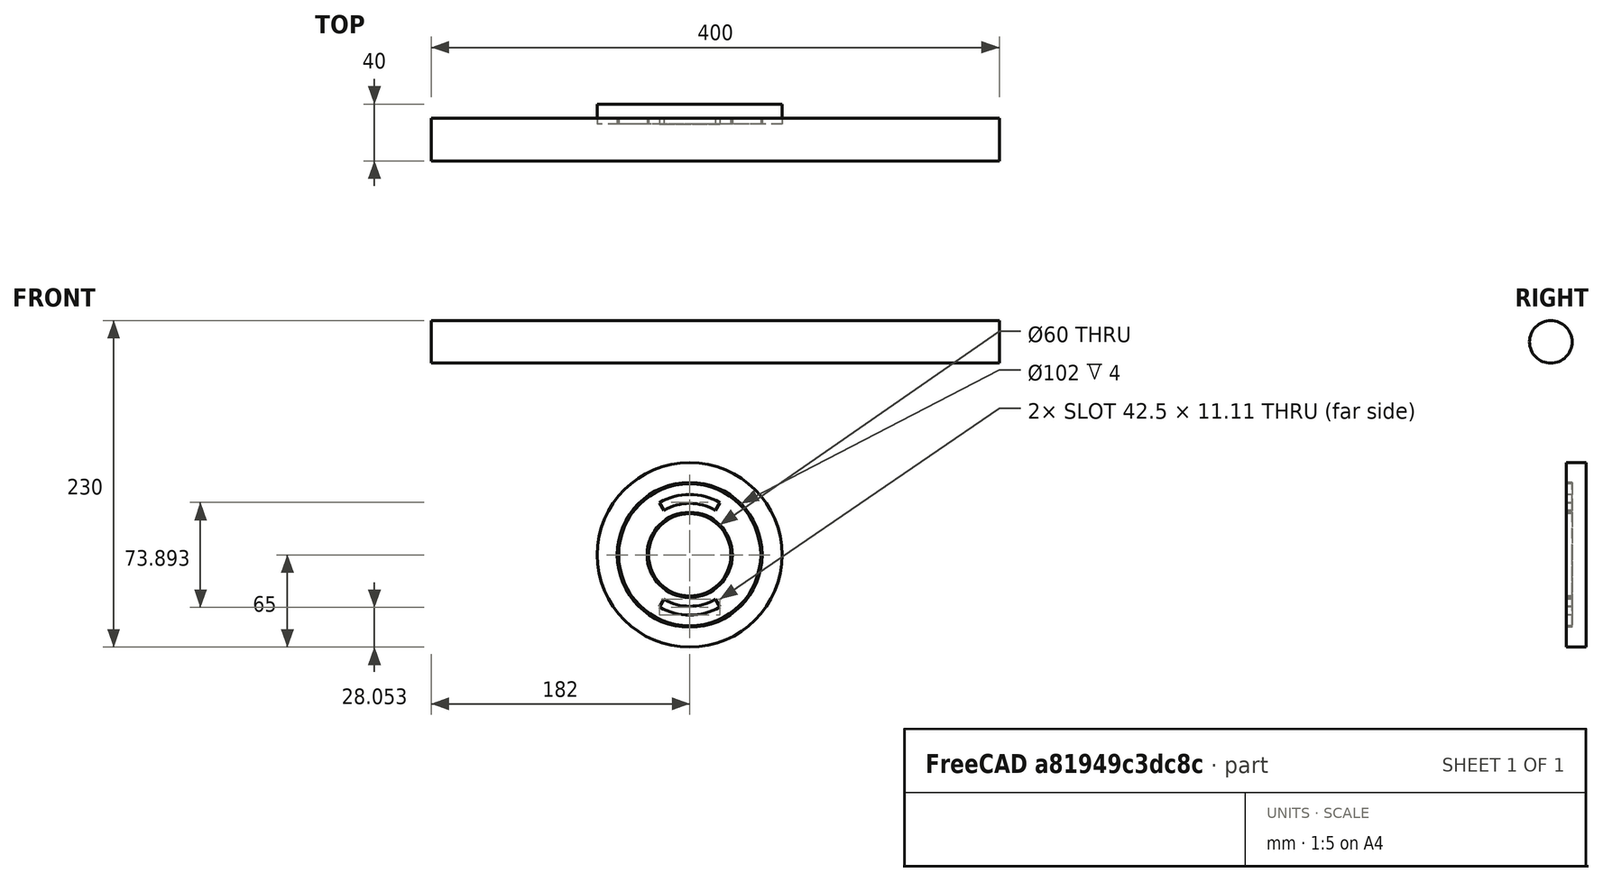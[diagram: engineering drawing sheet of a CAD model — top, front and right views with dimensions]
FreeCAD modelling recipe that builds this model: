
FCSTD DOCUMENT  (FreeCAD 0.19R24276 (Git))
Label: cameraMount
License: All rights reserved
LicenseURL: http://en.wikipedia.org/wiki/All_rights_reserved
objects: Part::Cylinder×9, Part::Cut×4, Part::MultiFuse×2, Part::FeaturePython×1
note: 16 computed .brp shape members not serialized (recipe doc carries the construction recipe); baked Part::Feature solids carry a one-line shape summary decoded from their .brp

FEATURE [Part::Cylinder] Cylinder  label="hor"
  Angle = 360
  AttacherType = Attacher::AttachEngine3D
  Height = 400
  Placement = pos=(0,0,150) rot=(0.707107,0,0.707107;3.14159rad)
  Radius = 15
FEATURE [Part::Cylinder] Cylinder001  label="Cylinder"
  Angle = 360
  AttacherType = Attacher::AttachEngine3D
  Height = 4
  Placement = pos=(182,-19,-4.2e-15) rot=(-1,0,0;4.71239rad)
  Radius = 50
FEATURE [Part::Cylinder] Cylinder002
  Angle = 360
  AttacherType = Attacher::AttachEngine3D
  Height = 4.5
  Placement = pos=(182,-19,-4e-15) rot=(1,0,0;1.5708rad)
  Radius = 30
FEATURE [Part::Cut] Cut  label="cameraPlate"
  Base = -> Cylinder001
  Tool = -> Cylinder002
FEATURE [Part::Cylinder] Cylinder003
  Angle = 60
  AttacherType = Attacher::AttachEngine3D
  Height = 4.5
  Placement = pos=(182,-19,-4e-15) rot=(-0.377964,-0.654654,0.654654;3.86433rad)
  Radius = 36.25
FEATURE [Part::Cylinder] Cylinder004
  Angle = 60
  AttacherType = Attacher::AttachEngine3D
  Height = 4.5
  Placement = pos=(182,-19,-4e-15) rot=(-0.377964,-0.654654,0.654654;3.86433rad)
  Radius = 42.5
FEATURE [Part::Cylinder] Cylinder005
  Angle = 60
  AttacherType = Attacher::AttachEngine3D
  Height = 4.5
  Placement = pos=(182,-19,-4e-15) rot=(0.774597,-0.447214,0.447214;1.82348rad)
  Radius = 42.5
FEATURE [Part::Cylinder] Cylinder006
  Angle = 60
  AttacherType = Attacher::AttachEngine3D
  Height = 4.5
  Placement = pos=(182,-19,-4e-15) rot=(0.774597,-0.447214,0.447214;1.82348rad)
  Radius = 36.25
FEATURE [Part::Cut] Cut001
  Base = -> Cylinder004
  Tool = -> Cylinder003
FEATURE [Part::Cut] Cut002
  Base = -> Cylinder005
  Tool = -> Cylinder006
FEATURE [Part::MultiFuse] Fusion
  Shapes = -> [Cut002,Cut001]
FEATURE [Part::Cut] Cut003  label="cameraPlate001"
  Base = -> Cut
  Placement = pos=(0,34,0) rot=(0,0,1;0rad)
  Tool = -> Fusion
FEATURE [Part::Cylinder] Cylinder007
  Angle = 360
  AttacherType = Attacher::AttachEngine3D
  Height = 10
  Placement = pos=(182,25,-1.38e-14) rot=(1,0,0;1.5708rad)
  Radius = 65
FEATURE [Part::Cylinder] Cylinder008
  Angle = 360
  AttacherType = Attacher::AttachEngine3D
  Height = 4
  Placement = pos=(182,15,-1.14e-14) rot=(1,0,0;1.5708rad)
  Radius = 29
FEATURE [Part::FeaturePython] Tube  # WARN: FeaturePython — macro-defined, semantics opaque (R4)
  AttacherType = Attacher::AttachEngine3D
  Height = 4
  InnerRadius = 51
  OuterRadius = 65
  Placement = pos=(182,15,-3.3e-15) rot=(1,0,0;1.5708rad)
FEATURE [Part::MultiFuse] Fusion001  label="camBack"
  Shapes = -> [Tube,Cylinder007,Cylinder008]
